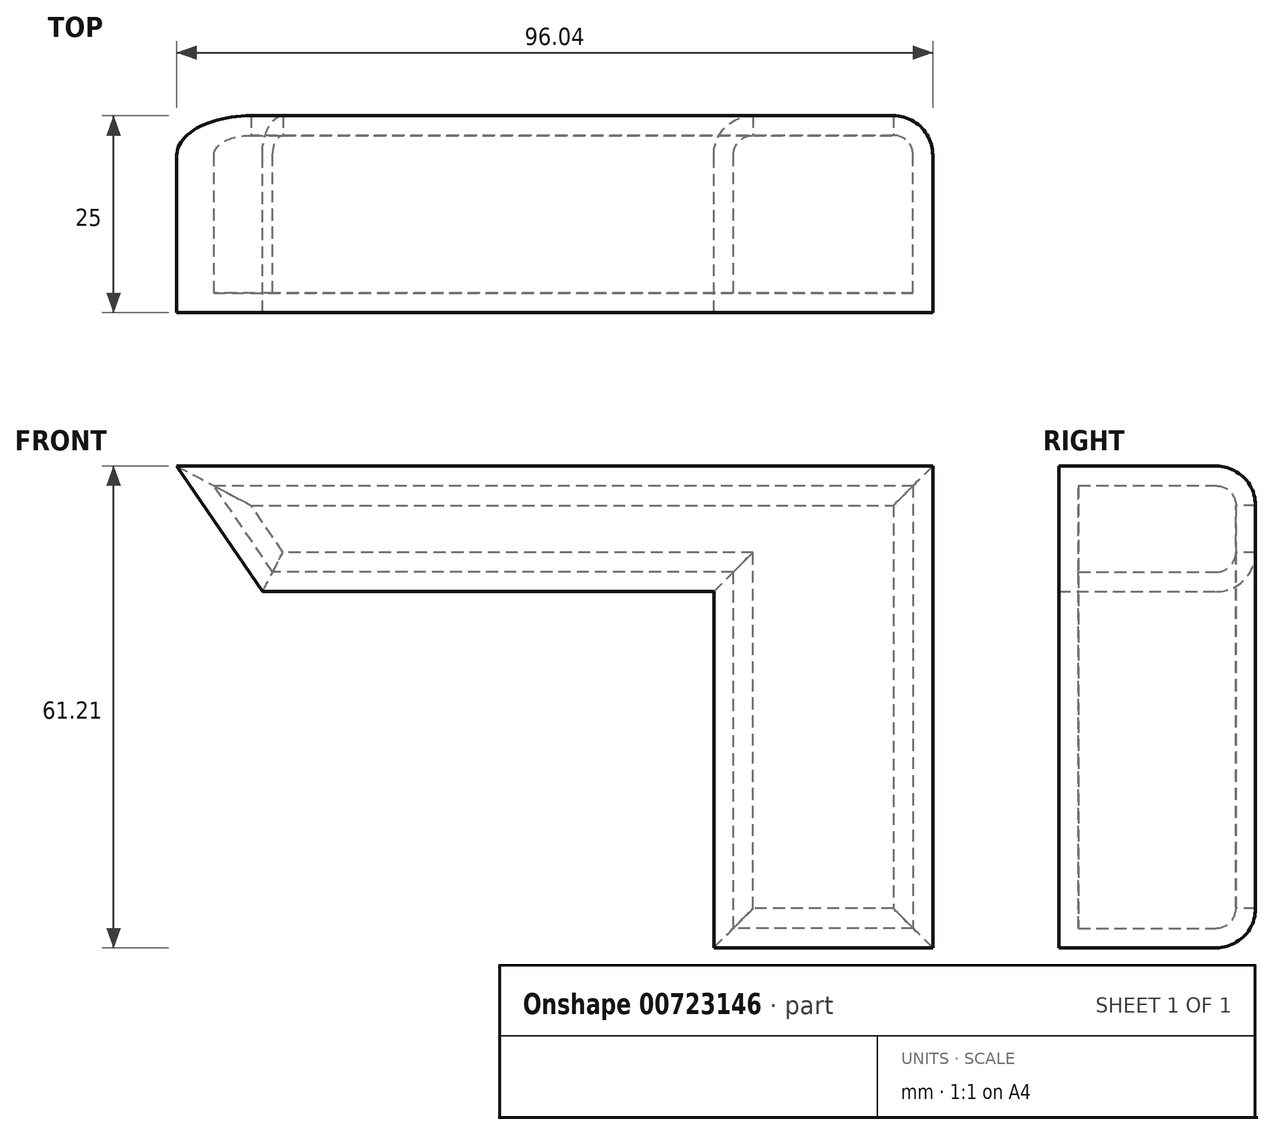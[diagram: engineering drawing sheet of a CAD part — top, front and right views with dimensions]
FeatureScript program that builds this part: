
annotation { "Feature Type Name" : "Feature", "Feature Type Description" : "" }
export const myFeature = defineFeature(function(context is Context, id is Id, definition is map)
    precondition{}
    {
        {
            var Q0;
            Q0=qCreatedBy(makeId("Front.planeOp"),FACE);
            var sketch = newSketch(context, id + "F0", { "sketchPlane" : qUnion([Q0])});
            skLineSegment(sketch, "E0", {"start": v(-49.23, 39.68) * mm, "end": v(46.81, 39.68) * mm});
            skLineSegment(sketch, "E1", {"start": v(46.81, 39.68) * mm, "end": v(46.81, -21.53) * mm});
            skLineSegment(sketch, "E2", {"start": v(46.81, -21.53) * mm, "end": v(19, -21.53) * mm});
            skLineSegment(sketch, "E3", {"start": v(19, -21.53) * mm, "end": v(19, 23.7) * mm});
            skLineSegment(sketch, "E4", {"start": v(19, 23.7) * mm, "end": v(-38.35, 23.7) * mm});
            skLineSegment(sketch, "E5", {"start": v(-38.35, 23.7) * mm, "end": v(-49.23, 39.68) * mm});
            skSolve(sketch);
        }
        {
            var Q0;
            Q0=makeQuery(id+"F0.imprint","IMPRINT",FACE,{"disambiguationData":[TD([[makeQuery(id+"F0.imprint","IMPRINT",EDGE,{"derivedFrom":sQuery(id+"F0.wireOp",EDGE,"E0")}),-1.0]])]});
            extrude(context, id + "F1", {"entities" : qUnion([Q0]), "depth" : 25 * mm, "offsetDistance" : 25 * mm});
        }
        {
            var Q0;
            Q0=makeQuery(id+"F1.opExtrude","CAP_EDGE",EDGE,{"disambiguationData":[OSD([sQuery(id+"F0.wireOp",EDGE,"E0")])],"isStart":true});
            var Q1;
            Q1=makeQuery(id+"F1.opExtrude","CAP_EDGE",EDGE,{"disambiguationData":[OSD([sQuery(id+"F0.wireOp",EDGE,"E1")])],"isStart":true});
            var Q2;
            Q2=makeQuery(id+"F1.opExtrude","CAP_EDGE",EDGE,{"disambiguationData":[OSD([sQuery(id+"F0.wireOp",EDGE,"E2")])],"isStart":true});
            var Q3;
            Q3=makeQuery(id+"F1.opExtrude","CAP_EDGE",EDGE,{"disambiguationData":[OSD([sQuery(id+"F0.wireOp",EDGE,"E4")])],"isStart":true});
            var Q4;
            Q4=makeQuery(id+"F1.opExtrude","CAP_EDGE",EDGE,{"disambiguationData":[OSD([sQuery(id+"F0.wireOp",EDGE,"E3")])],"isStart":true});
            var Q5;
            Q5=makeQuery(id+"F1.opExtrude","CAP_EDGE",EDGE,{"disambiguationData":[OSD([sQuery(id+"F0.wireOp",EDGE,"E5")])],"isStart":true});
            fillet(context, id + "F2", {"entities" : qUnion([Q0, Q1, Q2, Q3, Q4, Q5]), "radius" : 5 * mm, "tangentPropagation" : true, "allowEdgeOverflow" : false});
        }
        {
            var Q0;
            Q0=makeQuery(id+"F1.opExtrude","CAP_FACE",FACE,{"disambiguationData":[OSD([sQuery(id+"F0.wireOp",EDGE,"E0"),sQuery(id+"F0.wireOp",EDGE,"E1"),sQuery(id+"F0.wireOp",EDGE,"E2"),sQuery(id+"F0.wireOp",EDGE,"E3"),sQuery(id+"F0.wireOp",EDGE,"E4"),sQuery(id+"F0.wireOp",EDGE,"E5")])],"isStart":true});
            shell(context, id + "F3", {"entities" : qUnion([Q0]), "thickness" : 2.5 * mm});
        }
    });
